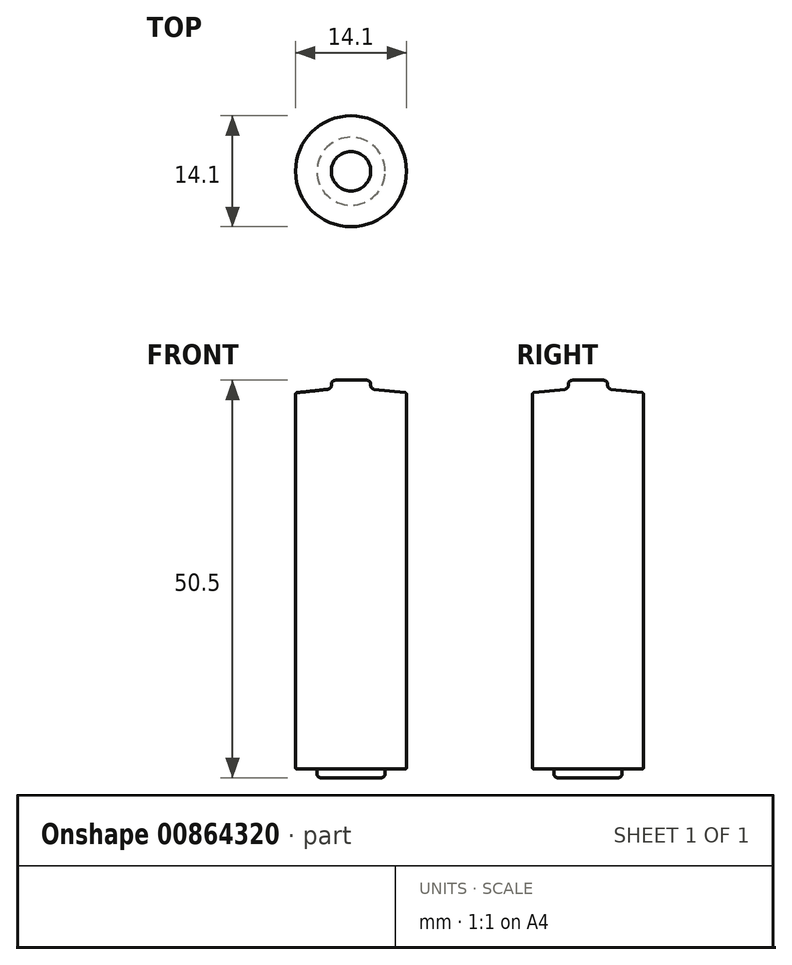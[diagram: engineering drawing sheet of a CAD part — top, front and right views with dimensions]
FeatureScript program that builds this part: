
annotation { "Feature Type Name" : "Feature", "Feature Type Description" : "" }
export const myFeature = defineFeature(function(context is Context, id is Id, definition is map)
    precondition{}
    {
        {
            var Q0;
            Q0=qCreatedBy(makeId("Top.planeOp"),FACE);
            var sketch = newSketch(context, id + "F0", { "sketchPlane" : qUnion([Q0])});
            skCircle(sketch, "E0", {"center": v(0, 0) * mm, "radius": 7.05 * mm});
            skSolve(sketch);
        }
        {
            var Q0;
            Q0=makeQuery(id+"F0.imprint","IMPRINT",FACE,{"disambiguationData":[TD([[makeQuery(id+"F0.imprint","IMPRINT",EDGE,{"derivedFrom":sQuery(id+"F0.wireOp",EDGE,"E0")}),1.0]])]});
            extrude(context, id + "F1", {"entities" : qUnion([Q0]), "depth" : 47.8 * mm, "offsetDistance" : 25 * mm});
        }
        {
            var Q0;
            Q0=makeQuery(id+"F1.opExtrude","CAP_FACE",FACE,{"disambiguationData":[OSD([sQuery(id+"F0.wireOp",EDGE,"E0")])],"isStart":true});
            var sketch = newSketch(context, id + "F2", { "sketchPlane" : qUnion([Q0])});
            skCircle(sketch, "E1", {"center": v(0, 0) * mm, "radius": 4.33 * mm});
            skSolve(sketch);
        }
        {
            var Q0;
            Q0=makeQuery(id+"F2.imprint","IMPRINT",FACE,{"disambiguationData":[TD([[makeQuery(id+"F2.imprint","IMPRINT",EDGE,{"derivedFrom":sQuery(id+"F2.wireOp",EDGE,"E1")}),1.0]])]});
            extrude(context, id + "F3", {"entities" : qUnion([Q0]), "operationType" : NewBodyOperationType.ADD, "depth" : 1.1 * mm, "offsetDistance" : 25 * mm});
        }
        {
            var Q0;
            Q0=makeQuery(id+"F1.opExtrude","CAP_FACE",FACE,{"disambiguationData":[OSD([sQuery(id+"F0.wireOp",EDGE,"E0")])],"isStart":false});
            var sketch = newSketch(context, id + "F4", { "sketchPlane" : qUnion([Q0])});
            skCircle(sketch, "E2", {"center": v(0, 0) * mm, "radius": 2.5 * mm});
            skSolve(sketch);
        }
        {
            var Q0;
            Q0 = qSketchRegion(id + "F4", true);
            extrude(context, id + "F5", {"entities" : qUnion([Q0]), "operationType" : NewBodyOperationType.ADD, "depth" : 0.5 * mm, "offsetDistance" : 25 * mm});
        }
        {
            var Q0;
            Q0=makeQuery(id+"F1.opExtrude","CAP_FACE",FACE,{"disambiguationData":[OSD([sQuery(id+"F0.wireOp",EDGE,"E0")])],"isStart":false});
            var sketch = newSketch(context, id + "F6", { "sketchPlane" : qUnion([Q0])});
            skCircle(sketch, "E3.0", {"center": v(0, 0) * mm, "radius": 7.05 * mm});
            skSolve(sketch);
        }
        {
            var Q0;
            Q0=makeQuery(id+"F5.opExtrude","CAP_FACE",FACE,{"disambiguationData":[OSD([sQuery(id+"F4.wireOp",EDGE,"E2")])],"isStart":false});
            var sketch = newSketch(context, id + "F7", { "sketchPlane" : qUnion([Q0])});
            skCircle(sketch, "E4.0", {"center": v(0, 0) * mm, "radius": 2.5 * mm});
            skSolve(sketch);
        }
        {
            var Q0;
            Q0 = qSketchRegion(id + "F6", true);
            var Q1;
            Q1 = qSketchRegion(id + "F7", true);
            loft(context, id + "F8", {"operationType" : NewBodyOperationType.ADD, "sheetProfilesArray" : [{ "sheetProfileEntities" : qUnion([Q0]) }, { "sheetProfileEntities" : qUnion([Q1]) }]});
        }
        {
            var Q0;
            Q0 = qSketchRegion(id + "F7", true);
            extrude(context, id + "F9", {"entities" : qUnion([Q0]), "operationType" : NewBodyOperationType.ADD, "depth" : 1.1 * mm, "offsetDistance" : 25 * mm});
        }
        {
            var Q0;
            Q0=makeQuery(id+"F3.opExtrude","CAP_EDGE",EDGE,{"disambiguationData":[OSD([sQuery(id+"F2.wireOp",EDGE,"E1")])],"isStart":false});
            fillet(context, id + "F10", {"entities" : qUnion([Q0]), "tangentPropagation" : true, "radius" : 0.5 * mm, "defaultsChanged" : true, "vertexSettings" : [], "allowEdgeOverflow" : false});
        }
        {
            var Q0;
            Q0=makeQuery(id+"F9.opExtrude","CAP_EDGE",EDGE,{"disambiguationData":[OSD([sQuery(id+"F7.wireOp",EDGE,"E4.0")])],"isStart":false});
            fillet(context, id + "F11", {"entities" : qUnion([Q0]), "tangentPropagation" : true, "radius" : 0.5 * mm, "defaultsChanged" : true, "vertexSettings" : [], "allowEdgeOverflow" : false});
        }
        {
            var Q0;
            {var subQ0=sQuery(id+"F7.wireOp",EDGE,"E4.0");Q0=makeQuery(id+"F9.boolean.opBoolean","MERGE",EDGE,{"derivedFrom":[makeQuery(id+"F8.boolean.opBoolean","MERGE",EDGE,{"derivedFrom":[makeQuery(id+"F5.opExtrude","CAP_EDGE",EDGE,{"disambiguationData":[OSD([sQuery(id+"F4.wireOp",EDGE,"E2")])],"isStart":false}),makeQuery(id+"F8.opLoft","MID_CAP_EDGE",EDGE,{"disambiguationData":[OSD([subQ0])],"capPos":1.0})]}),makeQuery(id+"F9.opExtrude","CAP_EDGE",EDGE,{"disambiguationData":[OSD([subQ0])],"isStart":true})]});}
            fillet(context, id + "F12", {"entities" : qUnion([Q0]), "tangentPropagation" : true, "radius" : 0.5 * mm, "defaultsChanged" : true, "vertexSettings" : [], "allowEdgeOverflow" : false});
        }
        {
            var Q0;
            Q0=makeQuery(id+"F8.boolean.opBoolean","MERGE",EDGE,{"derivedFrom":[makeQuery(id+"F1.opExtrude","CAP_EDGE",EDGE,{"disambiguationData":[OSD([sQuery(id+"F0.wireOp",EDGE,"E0")])],"isStart":false}),makeQuery(id+"F8.opLoft","MID_CAP_EDGE",EDGE,{"disambiguationData":[OSD([sQuery(id+"F6.wireOp",EDGE,"E3.0")])],"capPos":0.0})]});
            fillet(context, id + "F13", {"entities" : qUnion([Q0]), "tangentPropagation" : true, "radius" : 0.2 * mm, "defaultsChanged" : true, "vertexSettings" : [], "allowEdgeOverflow" : false});
        }
        {
            var Q0;
            Q0=makeQuery(id+"F1.opExtrude","CAP_EDGE",EDGE,{"disambiguationData":[OSD([sQuery(id+"F0.wireOp",EDGE,"E0")])],"isStart":true});
            fillet(context, id + "F14", {"entities" : qUnion([Q0]), "tangentPropagation" : true, "radius" : 0.2 * mm, "defaultsChanged" : true, "vertexSettings" : [], "allowEdgeOverflow" : false});
        }
    });
